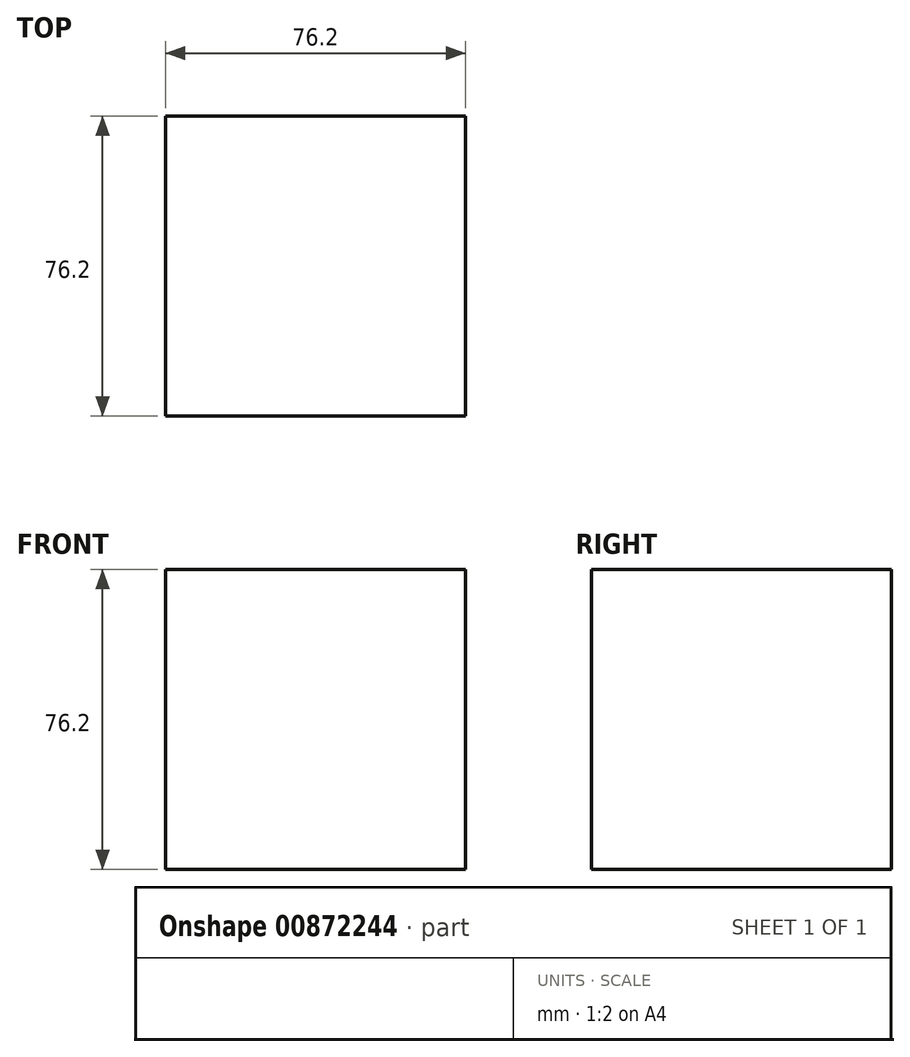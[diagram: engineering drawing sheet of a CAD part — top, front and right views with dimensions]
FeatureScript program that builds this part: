
annotation { "Feature Type Name" : "Feature", "Feature Type Description" : "" }
export const myFeature = defineFeature(function(context is Context, id is Id, definition is map)
    precondition{}
    {
        {
            var Q0;
            Q0=qCreatedBy(makeId("Top.planeOp"),FACE);
            var sketch = newSketch(context, id + "F0", { "sketchPlane" : qUnion([Q0])});
            skLineSegment(sketch, "E0.bottom", {"start": v(-71.4, 67.72) * mm, "end": v(4.8, 67.72) * mm});
            skLineSegment(sketch, "E0.top", {"start": v(-71.4, -8.48) * mm, "end": v(4.8, -8.48) * mm});
            skLineSegment(sketch, "E0.left", {"start": v(-71.4, 67.72) * mm, "end": v(-71.4, -8.48) * mm});
            skLineSegment(sketch, "E0.right", {"start": v(4.8, 67.72) * mm, "end": v(4.8, -8.48) * mm});
            skSolve(sketch);
        }
        {
            var Q0;
            Q0=makeQuery(id+"F0.imprint","IMPRINT",FACE,{"disambiguationData":[TD([[makeQuery(id+"F0.imprint","IMPRINT",EDGE,{"derivedFrom":sQuery(id+"F0.wireOp",EDGE,"E0.bottom")}),-1.0]])]});
            extrude(context, id + "F1", {"entities" : qUnion([Q0]), "depth" : 76.2 * mm, "offsetDistance" : 25.4 * mm});
        }
    });
